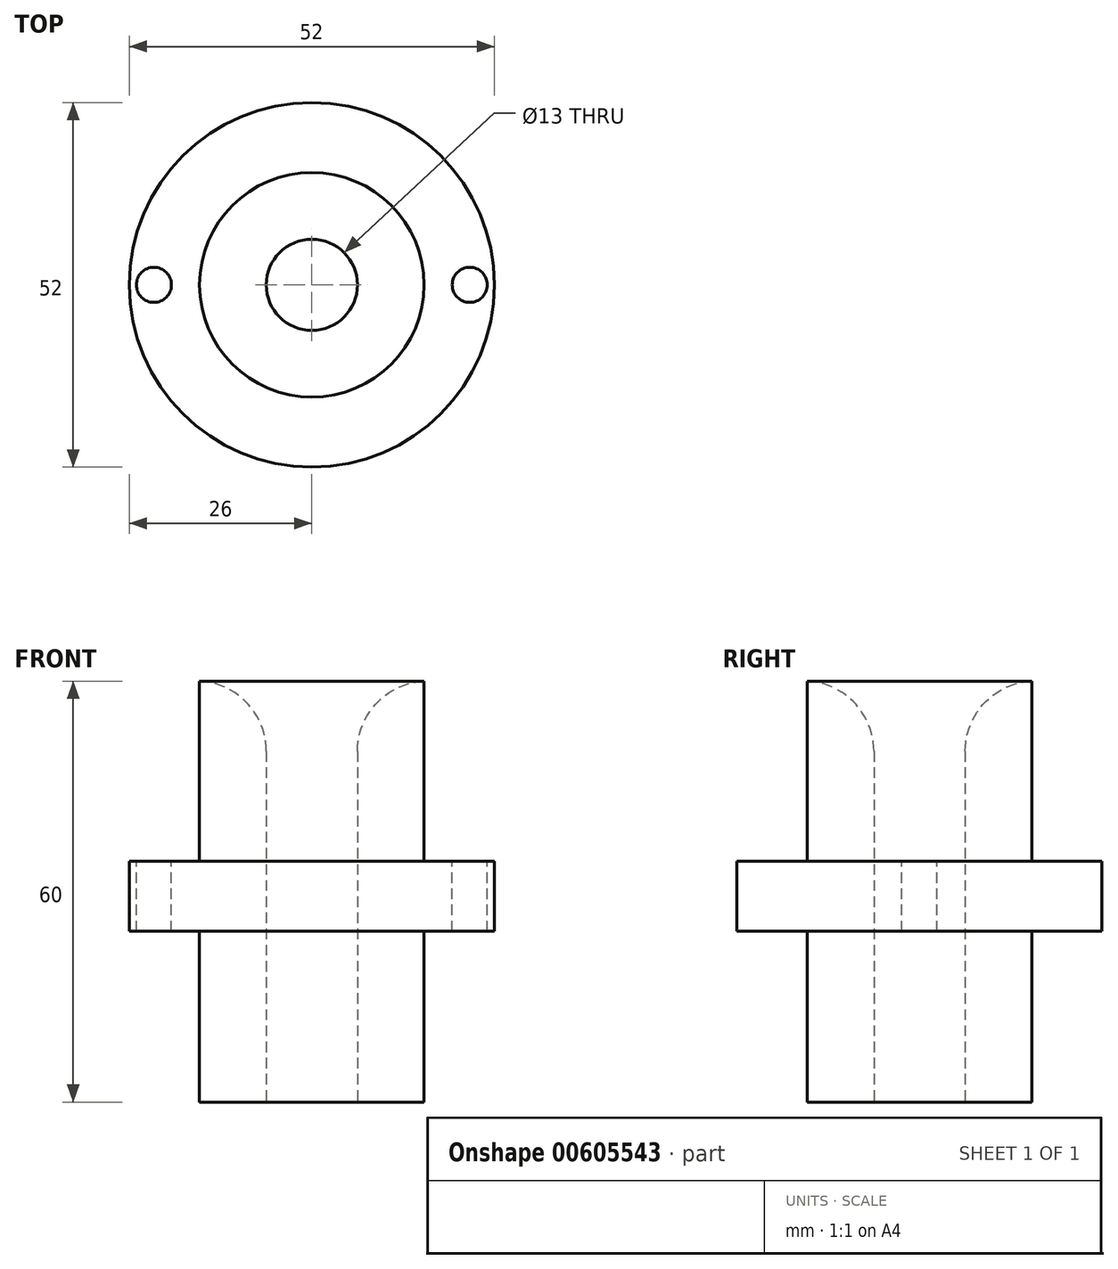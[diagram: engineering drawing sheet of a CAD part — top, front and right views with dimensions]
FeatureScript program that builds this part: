
annotation { "Feature Type Name" : "Feature", "Feature Type Description" : "" }
export const myFeature = defineFeature(function(context is Context, id is Id, definition is map)
    precondition{}
    {
        {
            var Q0;
            Q0=qCreatedBy(makeId("Front.planeOp"),FACE);
            var sketch = newSketch(context, id + "F0", { "sketchPlane" : qUnion([Q0])});
            skLineSegment(sketch, "E0", {"start": v(0, 0) * mm, "end": v(6.5, 0) * mm});
            skLineSegment(sketch, "E1", {"start": v(6.5, 0) * mm, "end": v(6.5, 50.01) * mm});
            skLineSegment(sketch, "E2", {"start": v(16, 62.39) * mm, "end": v(16, 34.34) * mm});
            skLineSegment(sketch, "E3", {"start": v(16, 34.34) * mm, "end": v(26, 34.34) * mm});
            skLineSegment(sketch, "E4", {"start": v(26, 34.34) * mm, "end": v(26, 24.34) * mm});
            skLineSegment(sketch, "E5", {"start": v(26, 24.34) * mm, "end": v(16, 24.34) * mm});
            skLineSegment(sketch, "E6", {"start": v(16, 24.34) * mm, "end": v(16, 0) * mm});
            skLineSegment(sketch, "E7", {"start": v(16, 0) * mm, "end": v(6.5, 0) * mm});
            skPoint(sketch, "E8.visualSharp", {"position": v(6.5, 64.86) * mm});
            skArc(sketch, "E8.filletArc", {"start": v(16, 60) * mm, "mid": v(9.25, 56.9) * mm, "end": v(6.5, 50.01) * mm});
            skSolve(sketch);
        }
        {
            var Q0;
            Q0=qCreatedBy(makeId("Front.planeOp"),FACE);
            var sketch = newSketch(context, id + "F1", { "sketchPlane" : qUnion([Q0])});
            skLineSegment(sketch, "E9", {"start": v(0, 0) * mm, "end": v(0, 70.42) * mm});
            skSolve(sketch);
        }
        {
            var Q0;
            Q0=makeQuery(id+"F0.imprint","IMPRINT",FACE,{"disambiguationData":[TD([[makeQuery(id+"F0.imprint","IMPRINT",EDGE,{"derivedFrom":sQuery(id+"F0.wireOp",EDGE,"E1")}),-1.0]])]});
            var Q1;
            Q1=sQuery(id+"F1.wireOp",EDGE,"E9");
            revolve(context, id + "F2", {"entities" : qUnion([Q0]), "axis" : qUnion([Q1]), "revolveType" : RevolveType.FULL});
        }
        {
            var Q0;
            Q0=makeQuery(id+"F2.opRevolve","SWEPT_FACE",FACE,{"disambiguationData":[OSD([sQuery(id+"F0.wireOp",EDGE,"E3")])]});
            var sketch = newSketch(context, id + "F3", { "sketchPlane" : qUnion([Q0])});
            skCircle(sketch, "E10", {"center": v(22.5, 0) * mm, "radius": 2.5 * mm});
            skCircle(sketch, "E11", {"center": v(-22.5, 0) * mm, "radius": 2.5 * mm});
            skSolve(sketch);
        }
        {
            var Q0;
            Q0=sQuery(id+"F3.wireOp",VERTEX,"E11.center");
            var Q1;
            Q1=sQuery(id+"F3.wireOp",VERTEX,"E10.center");
            var Q2;
            Q2=makeQuery(id+"F2.opRevolve","SWEPT_BODY",BODY,{"disambiguationData":[OSD([sQuery(id+"F0.wireOp",EDGE,"E1"),sQuery(id+"F0.wireOp",EDGE,"E2"),sQuery(id+"F0.wireOp",EDGE,"E3"),sQuery(id+"F0.wireOp",EDGE,"E4"),sQuery(id+"F0.wireOp",EDGE,"E5"),sQuery(id+"F0.wireOp",EDGE,"E6"),sQuery(id+"F0.wireOp",EDGE,"E7"),sQuery(id+"F0.wireOp",EDGE,"E8.filletArc")])]});
            hole(context, id + "F4", {"style" : HoleStyle.SIMPLE, "endStyle" : HoleEndStyle.THROUGH, "holeDiameter" : 5 * mm, "majorDiameter" : 5 * mm, "isTappedThrough" : true, "tappedDepth" : 12 * mm, "tapClearance" : 3, "locations" : qUnion([Q0, Q1]), "scope" : qUnion([Q2])});
        }
    });
